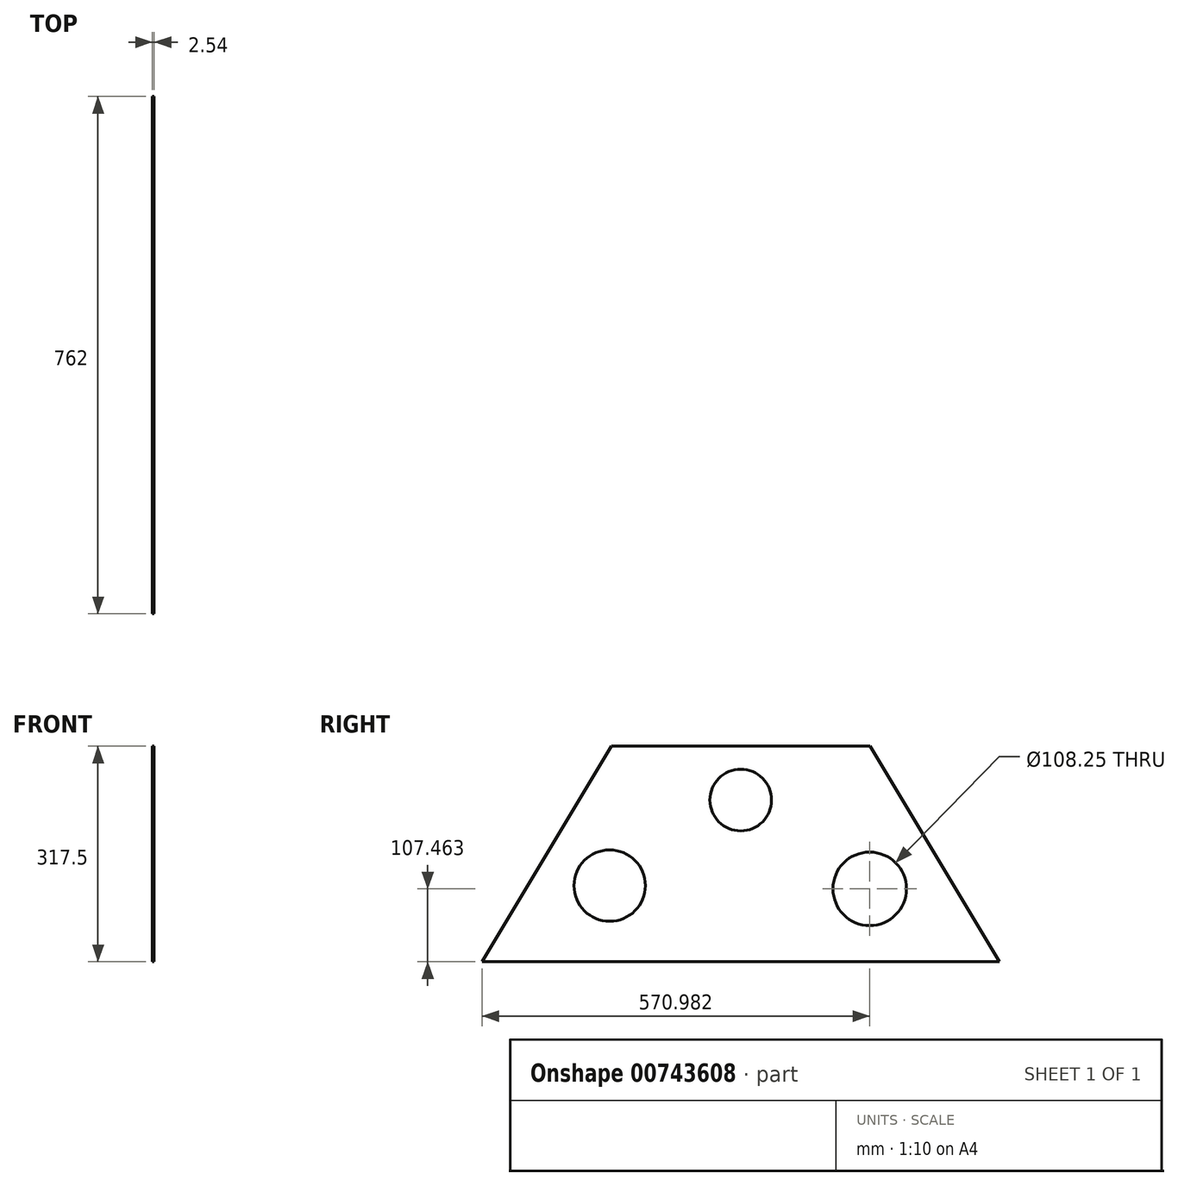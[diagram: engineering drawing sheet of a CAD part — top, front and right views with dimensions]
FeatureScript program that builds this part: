
annotation { "Feature Type Name" : "Feature", "Feature Type Description" : "" }
export const myFeature = defineFeature(function(context is Context, id is Id, definition is map)
    precondition{}
    {
        {
            var Q0;
            Q0=qCreatedBy(makeId("Right.planeOp"),FACE);
            var sketch = newSketch(context, id + "F0", { "sketchPlane" : qUnion([Q0])});
            skLineSegment(sketch, "E0", {"start": v(-190.5, 248.96) * mm, "end": v(190.5, 248.96) * mm});
            skLineSegment(sketch, "E1", {"start": v(-381, -68.54) * mm, "end": v(381, -68.54) * mm});
            skLineSegment(sketch, "E2", {"start": v(-190.5, 248.96) * mm, "end": v(-381, -68.54) * mm});
            skLineSegment(sketch, "E3", {"start": v(190.5, 248.96) * mm, "end": v(381, -68.54) * mm});
            skSolve(sketch);
        }
        {
            var Q0;
            Q0=makeQuery(id+"F0.imprint","IMPRINT",FACE,{"disambiguationData":[TD([[makeQuery(id+"F0.imprint","IMPRINT",EDGE,{"derivedFrom":sQuery(id+"F0.wireOp",EDGE,"E0")}),-1.0]])]});
            extrude(context, id + "F1", {"entities" : qUnion([Q0]), "depth" : 2.54 * mm, "offsetDistance" : 25.4 * mm});
        }
        {
            var Q0;
            Q0=makeQuery(id+"F1.opExtrude","CAP_FACE",FACE,{"disambiguationData":[OSD([sQuery(id+"F0.wireOp",EDGE,"E0"),sQuery(id+"F0.wireOp",EDGE,"E1"),sQuery(id+"F0.wireOp",EDGE,"E2"),sQuery(id+"F0.wireOp",EDGE,"E3")])],"isStart":true});
            var sketch = newSketch(context, id + "F2", { "sketchPlane" : qUnion([Q0])});
            skCircle(sketch, "E4", {"center": v(-189.98, 38.92) * mm, "radius": 54.12 * mm});
            skCircle(sketch, "E5", {"center": v(193.07, 43.67) * mm, "radius": 52.58 * mm});
            skCircle(sketch, "E6", {"center": v(0, 169.67) * mm, "radius": 45.45 * mm});
            skSolve(sketch);
        }
        {
            var Q0;
            Q0 = qSketchRegion(id + "F2", true);
            extrude(context, id + "F3", {"entities" : qUnion([Q0]), "operationType" : NewBodyOperationType.REMOVE, "endBound" : BoundingType.THROUGH_ALL, "oppositeDirection" : true, "depth" : 25.4 * mm, "offsetDistance" : 25.4 * mm});
        }
    });
